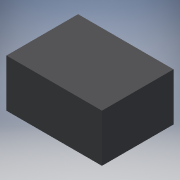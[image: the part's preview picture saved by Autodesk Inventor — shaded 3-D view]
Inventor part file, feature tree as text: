
AUTODESK INVENTOR PART (.ipt)
format: ipt  version: 2017 (Build 210142000, 142)  size: 84,480 bytes
history: native  units: mm
features: extrude x1, sketch x1
ambient origin geometry x8: Origin, YZ Plane, XZ Plane, XY Plane, X Axis, Y Axis, Z Axis, Center Point
bodies: Solid1 (feature_tree)
feature tree (2):
  extrude  "Extrusion1"  Depth=100.0mm
  sketch  "Sketch1"  dims[d0=200.0mm d1=100.0mm d2=150.0mm d3=0.0mm]
